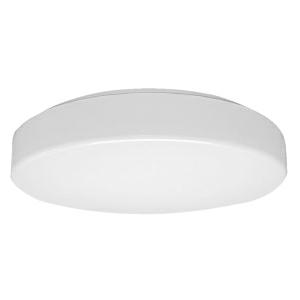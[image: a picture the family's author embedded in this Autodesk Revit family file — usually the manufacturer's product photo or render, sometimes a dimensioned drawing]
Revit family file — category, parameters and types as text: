
# Revit family: oblo_fit_-_oba_1000_830_00813344_93c8
name_source: partatom
category: Lighting Fixtures
units: mm (PartAtom-declared; Revit-internal decimal feet)

## family parameters
Cut with Voids When Loaded = No
Host = Face
Light Source = No
Part Type = Normal
Room Calculation Point = No
Round Connector Dimension = Use Diameter
Shared = No

## types (1)
- OBLO.fit - OBA 1000/830 (1 x LED, 1500 lm, 3000K)
    Apparent Load = 11 VA
    Approval mark = CE
    CIE Flux Codes = 41 72 91 84 100
    Color Rendering = 80-89
    Color Temperature = 3000K
    Control Gear = Electronic ballast
    Default Elevation = 1800 mm
    Description = OBA 1000/830|Surface-mounted luminaire.|light source:   Warm white   |work equipment: Power supply unit|luminous flux: 1500 lm|light distribution: Direct|class of protection: I|technology: Switchable|mains lead: Direct power supply|glare control: without|
    Frequency = 50 Hz, 60 Hz
    Height = 85 mm
    Lamp = 1 x LED
    Lamp Light Flux = 1500 lm
    Lamp count = 1
    Length = 300 mm
    Luminous efficacy = 136 lm/W
    Manufacturer = Waldmann
    ModVariant = No
    Model = 00813344
    Mounting Place = Ceiling
    Mounting Type = Surface mounted
    Number of Poles = 1
    OnlyDefault = Yes
    Power Factor = 1
    Product Name = OBLO.fit - OBA 1000/830
    Product group = Ceiling mounted luminaire
    ProductGroupID = 3
    Protection Class = Protection class I
    Protection Degree = IP 40
    RLX_Detail_Level = 1
    RLX_Emergency_Light_Flux = 0 lm
    RLX_Emergency_Type = 0
    RLX_Emergency_Type_DB = No
    RlxData = <blob elided: 22145 chars, md5=b10375aa>
    Socket = socket
    Standby Power = 0 W
    System Light Flux = 1500 lm
    System Power = 11 W
    Type Comments = Product without accessories
    Type Image = oblo_led.jpg
    URL = http://relux.com
    VarID = ---
    Voltage = 230 V
    Voltage Range = 220-240 V
    Weight = 0.00 kg
    Width = 0 mm  [stored 0 ft]

note: [stored X ft] marks values corroborated as IEEE doubles in the binary element streams (Revit-internal decimal feet)

## geometry (parser evidence)
native form markers: Blend x4, Sweep x14
no freeform markers — native parametric forms only
